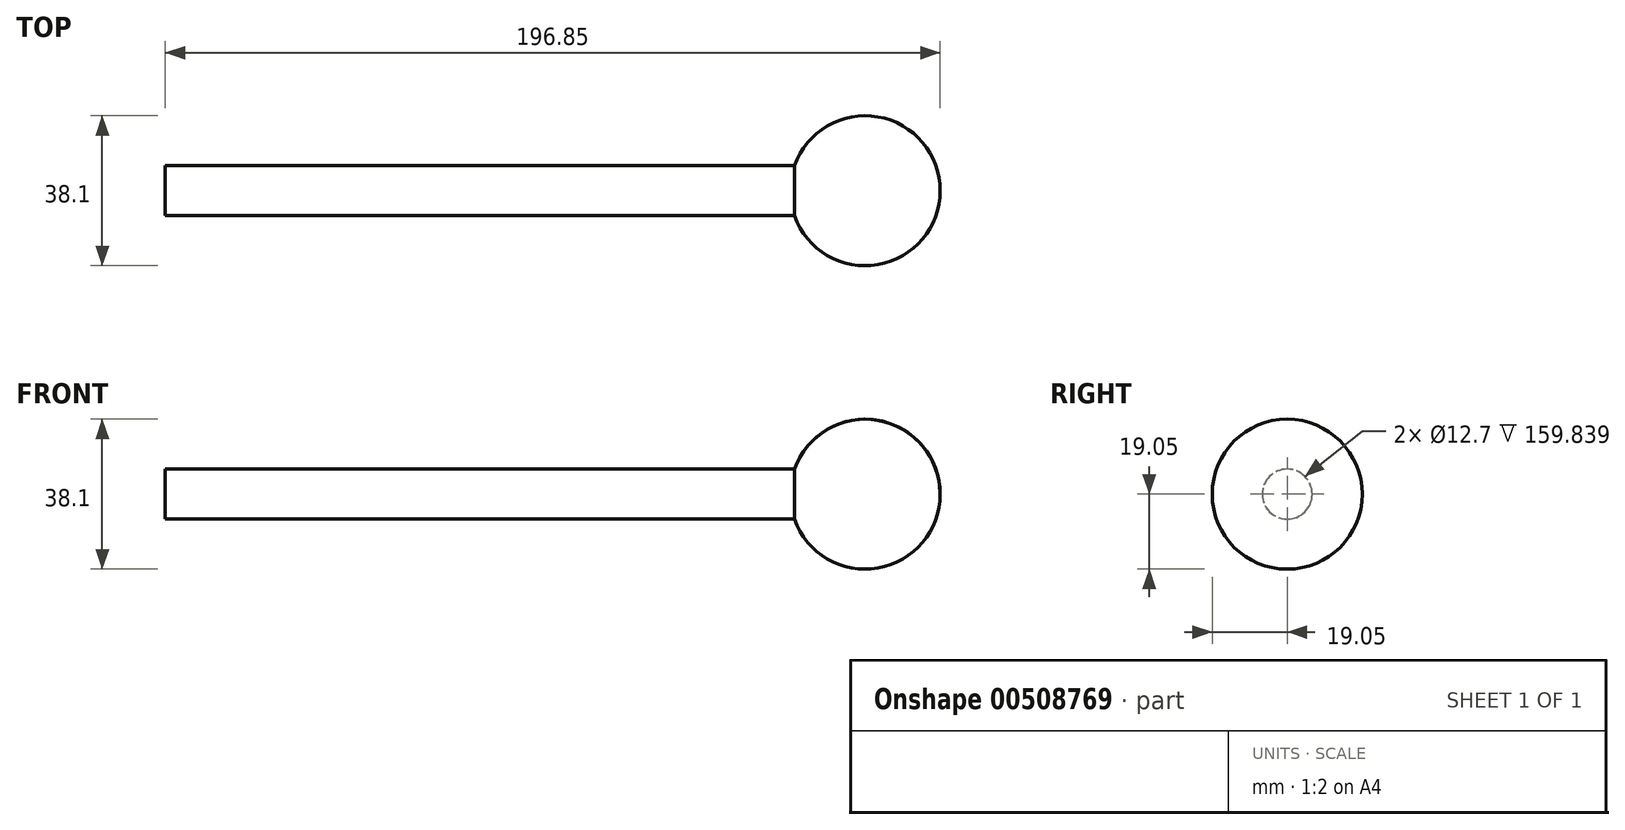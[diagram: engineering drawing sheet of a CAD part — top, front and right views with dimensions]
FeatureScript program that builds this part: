
annotation { "Feature Type Name" : "Feature", "Feature Type Description" : "" }
export const myFeature = defineFeature(function(context is Context, id is Id, definition is map)
    precondition{}
    {
        {
            var Q0;
            Q0=qCreatedBy(makeId("Front.planeOp"),FACE);
            var sketch = newSketch(context, id + "F0", { "sketchPlane" : qUnion([Q0])});
            skLineSegment(sketch, "E0", {"start": v(0, 0) * mm, "end": v(0, 6.35) * mm});
            skLineSegment(sketch, "E1", {"start": v(0, 6.35) * mm, "end": v(159.84, 6.35) * mm});
            skArc(sketch, "E2", {"start": v(196.85, 0) * mm, "mid": v(181.02, 18.78) * mm, "end": v(159.84, 6.35) * mm});
            skLineSegment(sketch, "E3", {"start": v(-77.38, 0) * mm, "end": v(234.73, 0) * mm});
            skSolve(sketch);
        }
        {
            var Q0;
            Q0=sQuery(id+"F0.wireOp",EDGE,"E1");
            var Q1;
            Q1=sQuery(id+"F0.wireOp",EDGE,"E2");
            var Q2;
            Q2=sQuery(id+"F0.wireOp",EDGE,"E0");
            var Q3;
            Q3=sQuery(id+"F0.wireOp",EDGE,"E3");
            revolve(context, id + "F1", {"bodyType" : ToolBodyType.SURFACE, "surfaceEntities" : qUnion([Q0, Q1, Q2]), "axis" : qUnion([Q3]), "revolveType" : RevolveType.FULL});
        }
    });
